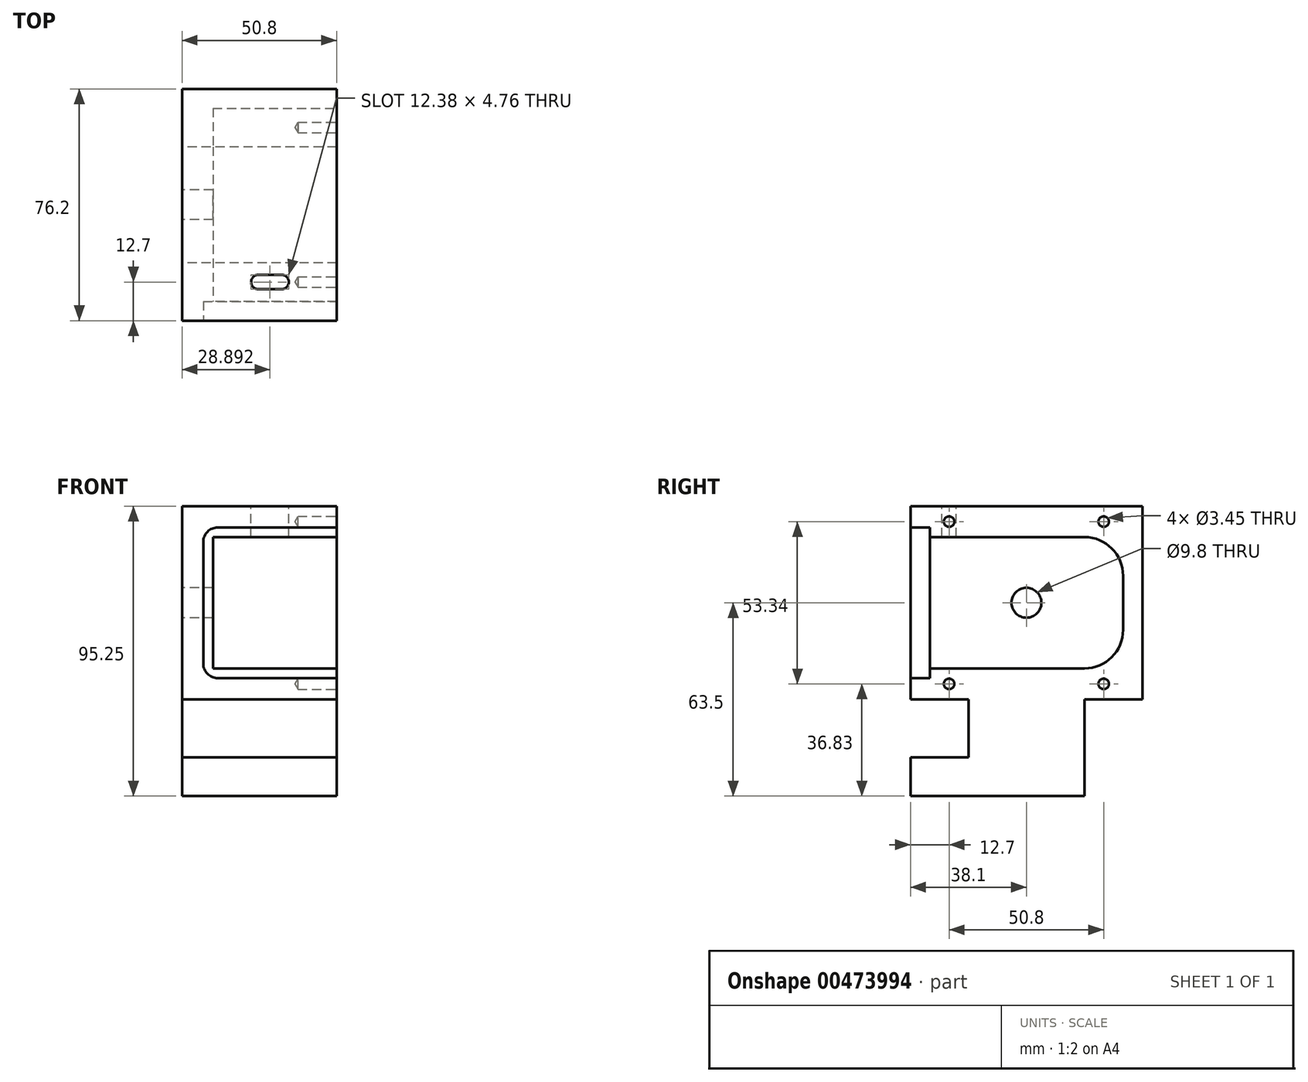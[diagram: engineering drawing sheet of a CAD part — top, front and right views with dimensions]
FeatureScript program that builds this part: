
annotation { "Feature Type Name" : "Feature", "Feature Type Description" : "" }
export const myFeature = defineFeature(function(context is Context, id is Id, definition is map)
    precondition{}
    {
        {
            var Q0;
            Q0=qCreatedBy(makeId("Right.planeOp"),FACE);
            var sketch = newSketch(context, id + "F0", { "sketchPlane" : qUnion([Q0])});
            skLineSegment(sketch, "E0.bottom", {"start": v(0, 0) * mm, "end": v(76.2, 0) * mm});
            skLineSegment(sketch, "E0.top", {"start": v(0, 63.5) * mm, "end": v(76.2, 63.5) * mm});
            skLineSegment(sketch, "E0.left", {"start": v(0, 0) * mm, "end": v(0, 63.5) * mm});
            skLineSegment(sketch, "E0.right", {"start": v(76.2, 0) * mm, "end": v(76.2, 63.5) * mm});
            skLineSegment(sketch, "E1.bottom", {"start": v(19.05, 0) * mm, "end": v(57.15, 0) * mm});
            skLineSegment(sketch, "E1.top", {"start": v(19.05, -19.05) * mm, "end": v(57.15, -19.05) * mm});
            skLineSegment(sketch, "E1.left", {"start": v(19.05, 0) * mm, "end": v(19.05, -19.05) * mm});
            skLineSegment(sketch, "E1.right", {"start": v(57.15, 0) * mm, "end": v(57.15, -19.05) * mm});
            skSolve(sketch);
        }
        {
            var Q0;
            Q0 = qSketchRegion(id + "F0", true);
            extrude(context, id + "F1", {"entities" : qUnion([Q0]), "depth" : 50.8 * mm});
        }
        {
            var Q0;
            Q0=makeQuery(id+"F1.opExtrude","CAP_FACE",FACE,{"disambiguationData":[OSD([sQuery(id+"F0.wireOp",EDGE,"E0.bottom"),sQuery(id+"F0.wireOp",EDGE,"E0.top"),sQuery(id+"F0.wireOp",EDGE,"E0.left"),sQuery(id+"F0.wireOp",EDGE,"E0.right"),sQuery(id+"F0.wireOp",EDGE,"E1.top"),sQuery(id+"F0.wireOp",EDGE,"E1.left"),sQuery(id+"F0.wireOp",EDGE,"E1.right")])],"isStart":true});
            var sketch = newSketch(context, id + "F2", { "sketchPlane" : qUnion([Q0])});
            skCircle(sketch, "E2", {"center": v(-38.1, 31.75) * mm, "radius": 11.22 * mm});
            skSolve(sketch);
        }
        {
            var Q0;
            Q0=sQuery(id+"F2.wireOp",VERTEX,"E2.center");
            var Q1;
            Q1=makeQuery(id+"F1.opExtrude","SWEPT_BODY",BODY,{"disambiguationData":[OSD([sQuery(id+"F0.wireOp",EDGE,"E0.bottom"),sQuery(id+"F0.wireOp",EDGE,"E0.top"),sQuery(id+"F0.wireOp",EDGE,"E0.left"),sQuery(id+"F0.wireOp",EDGE,"E0.right"),sQuery(id+"F0.wireOp",EDGE,"E1.top"),sQuery(id+"F0.wireOp",EDGE,"E1.left"),sQuery(id+"F0.wireOp",EDGE,"E1.right")])]});
            hole(context, id + "F3", {"style" : HoleStyle.SIMPLE, "endStyle" : HoleEndStyle.THROUGH, "standardTappedOrClearance" : lookupTablePath({ "standard" : "ANSI", "fit" : "Close", "size" : "3/8", "type" : "Clearance" }), "standardBlindInLast" : lookupTablePath({ "fit" : "Close", "standard" : "ANSI", "size" : "3/8", "type" : "Clearance" }), "holeDiameter" : 9.8 * mm, "isTappedThrough" : true, "tappedDepth" : 3.96 * mm, "tapClearance" : 3, "locations" : qUnion([Q0]), "scope" : qUnion([Q1])});
        }
        {
            var Q0;
            Q0=makeQuery(id+"F1.opExtrude","SWEPT_FACE",FACE,{"disambiguationData":[OSD([sQuery(id+"F0.wireOp",EDGE,"E1.top")])]});
            var sketch = newSketch(context, id + "F4", { "sketchPlane" : qUnion([Q0])});
            skLineSegment(sketch, "E3.0", {"start": v(50.8, -76.2) * mm, "end": v(0, -76.2) * mm});
            skLineSegment(sketch, "E4.0", {"start": v(50.8, -57.15) * mm, "end": v(50.8, -76.2) * mm});
            skLineSegment(sketch, "E5.0", {"start": v(50.8, -19.05) * mm, "end": v(50.8, -57.15) * mm});
            skLineSegment(sketch, "E6.0", {"start": v(50.8, 0) * mm, "end": v(50.8, -19.05) * mm});
            skLineSegment(sketch, "E7.bottom", {"start": v(0, 0) * mm, "end": v(50.8, 0) * mm});
            skLineSegment(sketch, "E7.top", {"start": v(0, -76.2) * mm, "end": v(50.8, -76.2) * mm});
            skLineSegment(sketch, "E7.left", {"start": v(0, 0) * mm, "end": v(0, -76.2) * mm});
            skLineSegment(sketch, "E7.right", {"start": v(50.8, 0) * mm, "end": v(50.8, -76.2) * mm});
            skSolve(sketch);
        }
        {
            var Q0;
            {var subQ0=sQuery(id+"F4.wireOp",EDGE,"E7.bottom");Q0=makeQuery(id+"F4.imprint","IMPRINT",FACE,{"disambiguationData":[TD([[makeQuery(id+"F4.imprint","IMPRINT",EDGE,{"derivedFrom":subQ0}),-1.0]])]});}
            var Q1;
            {var subQ0=sQuery(id+"F4.wireOp",EDGE,"E7.top");Q1=makeQuery(id+"F4.imprint","IMPRINT",FACE,{"disambiguationData":[TD([[makeQuery(id+"F4.imprint","IMPRINT",EDGE,{"derivedFrom":subQ0}),1.0]])]});}
            var Q2;
            {var subQ0=sQuery(id+"F0.wireOp",EDGE,"E1.top");var subQ3=makeQuery(id+"F1.opExtrude","SWEPT_EDGE",EDGE,{"disambiguationData":[OSD([subQ0,sQuery(id+"F0.wireOp",EDGE,"E1.left")])]});Q2=makeQuery(id+"F4.imprint","IMPRINT",FACE,{"disambiguationData":[TD([[makeQuery(id+"F4.imprint","IMPRINT",EDGE,{"derivedFrom":subQ3}),1.0]])]});}
            extrude(context, id + "F5", {"entities" : qUnion([Q0, Q1, Q2]), "operationType" : NewBodyOperationType.ADD, "depth" : 12.7 * mm});
        }
        {
            var Q0;
            Q0=makeQuery(id+"F1.opExtrude","SWEPT_FACE",FACE,{"disambiguationData":[OSD([sQuery(id+"F0.wireOp",EDGE,"E0.left")])]});
            var sketch = newSketch(context, id + "F6", { "sketchPlane" : qUnion([Q0])});
            skSolve(sketch);
        }
        {
            var Q0;
            {var subQ0=sQuery(id+"F0.wireOp",EDGE,"E0.left");Q0=makeQuery(id+"F6.imprint","IMPRINT",FACE,{"disambiguationData":[TD([[makeQuery(id+"F6.imprint","IMPRINT",EDGE,{"derivedFrom":makeQuery(id+"F1.opExtrude","CAP_EDGE",EDGE,{"disambiguationData":[OSD([subQ0])],"isStart":true})}),-1.0]])]});}
            var sketch = newSketch(context, id + "F7", { "sketchPlane" : qUnion([Q0])});
            skLineSegment(sketch, "E8.0.0", {"start": v(0, 63.5) * mm, "end": v(0, 0) * mm});
            skLineSegment(sketch, "E8.0.1", {"start": v(0, 0) * mm, "end": v(50.8, 0) * mm});
            skLineSegment(sketch, "E8.0.2", {"start": v(50.8, 0) * mm, "end": v(50.8, 63.5) * mm});
            skLineSegment(sketch, "E8.0.3", {"start": v(50.8, 63.5) * mm, "end": v(0, 63.5) * mm});
            skLineSegment(sketch, "E9.bottom", {"start": v(10.16, 53.34) * mm, "end": v(50.8, 53.34) * mm});
            skLineSegment(sketch, "E9.top", {"start": v(10.16, 10.16) * mm, "end": v(50.8, 10.16) * mm});
            skLineSegment(sketch, "E9.left", {"start": v(10.16, 53.34) * mm, "end": v(10.16, 10.16) * mm});
            skLineSegment(sketch, "E9.right", {"start": v(50.8, 53.34) * mm, "end": v(50.8, 10.16) * mm});
            skSolve(sketch);
        }
        {
            var Q0;
            Q0=makeQuery(id+"F7.imprint","IMPRINT",FACE,{"disambiguationData":[TD([[makeQuery(id+"F7.imprint","IMPRINT",EDGE,{"derivedFrom":sQuery(id+"F7.wireOp",EDGE,"E9.bottom")}),-1.0]])]});
            extrude(context, id + "F8", {"entities" : qUnion([Q0]), "operationType" : NewBodyOperationType.REMOVE, "oppositeDirection" : true, "depth" : 69.85 * mm});
        }
        {
            var Q0;
            {var subQ0=sQuery(id+"F0.wireOp",EDGE,"E0.left");Q0=makeQuery(id+"F6.imprint","IMPRINT",FACE,{"disambiguationData":[TD([[makeQuery(id+"F6.imprint","IMPRINT",EDGE,{"derivedFrom":makeQuery(id+"F1.opExtrude","CAP_EDGE",EDGE,{"disambiguationData":[OSD([subQ0])],"isStart":true})}),-1.0]])]});}
            var sketch = newSketch(context, id + "F9", { "sketchPlane" : qUnion([Q0])});
            skLineSegment(sketch, "E10.0.0", {"start": v(0, 63.5) * mm, "end": v(0, 0) * mm});
            skLineSegment(sketch, "E10.0.1", {"start": v(0, 0) * mm, "end": v(50.8, 0) * mm});
            skLineSegment(sketch, "E10.0.2", {"start": v(50.8, 0) * mm, "end": v(50.8, 63.5) * mm});
            skLineSegment(sketch, "E10.0.3", {"start": v(50.8, 63.5) * mm, "end": v(0, 63.5) * mm});
            skLineSegment(sketch, "E11.0", {"start": v(10.16, 53.34) * mm, "end": v(50.8, 53.34) * mm});
            skLineSegment(sketch, "E12.0", {"start": v(10.16, 53.34) * mm, "end": v(10.16, 10.16) * mm});
            skLineSegment(sketch, "E13.0", {"start": v(10.16, 10.16) * mm, "end": v(50.8, 10.16) * mm});
            skLineSegment(sketch, "E14.bottom", {"start": v(6.98, 56.51) * mm, "end": v(50.8, 56.51) * mm});
            skLineSegment(sketch, "E14.top", {"start": v(6.99, 6.99) * mm, "end": v(50.8, 6.99) * mm});
            skLineSegment(sketch, "E14.left", {"start": v(6.99, 56.51) * mm, "end": v(6.99, 6.99) * mm});
            skLineSegment(sketch, "E14.right", {"start": v(50.8, 56.51) * mm, "end": v(50.8, 6.99) * mm});
            skSolve(sketch);
        }
        {
            var Q0;
            {var subQ0=sQuery(id+"F9.wireOp",EDGE,"E11.0");Q0=makeQuery(id+"F9.imprint","IMPRINT",FACE,{"disambiguationData":[TD([[makeQuery(id+"F9.imprint","IMPRINT",EDGE,{"derivedFrom":subQ0}),-1.0]])]});}
            var Q1;
            {var subQ2=sQuery(id+"F9.wireOp",EDGE,"E11.0");Q1=makeQuery(id+"F9.imprint","IMPRINT",FACE,{"disambiguationData":[TD([[makeQuery(id+"F9.imprint","IMPRINT",EDGE,{"derivedFrom":subQ2}),1.0]])]});}
            extrude(context, id + "F10", {"entities" : qUnion([Q0, Q1]), "operationType" : NewBodyOperationType.REMOVE, "oppositeDirection" : true, "depth" : 6.35 * mm});
        }
        {
            var Q0;
            Q0=makeQuery(id+"F5.boolean.opBoolean","MERGE",FACE,{"derivedFrom":[makeQuery(id+"F1.opExtrude","CAP_FACE",FACE,{"disambiguationData":[OSD([sQuery(id+"F0.wireOp",EDGE,"E0.bottom"),sQuery(id+"F0.wireOp",EDGE,"E0.top"),sQuery(id+"F0.wireOp",EDGE,"E0.left"),sQuery(id+"F0.wireOp",EDGE,"E0.right"),sQuery(id+"F0.wireOp",EDGE,"E1.top"),sQuery(id+"F0.wireOp",EDGE,"E1.left"),sQuery(id+"F0.wireOp",EDGE,"E1.right")])],"isStart":false}),makeQuery(id+"F5.opExtrude","SWEPT_FACE",FACE,{"disambiguationData":[OSD([sQuery(id+"F4.wireOp",EDGE,"E7.right")])]})]});
            var sketch = newSketch(context, id + "F11", { "sketchPlane" : qUnion([Q0])});
            skLineSegment(sketch, "E15.bottom", {"start": v(0, -19.05) * mm, "end": v(76.2, -19.05) * mm});
            skLineSegment(sketch, "E15.top", {"start": v(0, -31.75) * mm, "end": v(76.2, -31.75) * mm});
            skLineSegment(sketch, "E15.left", {"start": v(0, -19.05) * mm, "end": v(0, -31.75) * mm});
            skLineSegment(sketch, "E15.right", {"start": v(76.2, -19.05) * mm, "end": v(76.2, -31.75) * mm});
            skSolve(sketch);
        }
        {
            var Q0;
            Q0=makeQuery(id+"F11.imprint","IMPRINT",FACE,{"disambiguationData":[TD([[makeQuery(id+"F11.imprint","IMPRINT",EDGE,{"derivedFrom":sQuery(id+"F11.wireOp",EDGE,"E15.top")}),1.0]])]});
            extrude(context, id + "F12", {"entities" : qUnion([Q0]), "operationType" : NewBodyOperationType.REMOVE, "oppositeDirection" : true, "depth" : 9.52 * mm});
        }
        {
            var Q0;
            Q0=makeQuery(id+"F5.boolean.opBoolean","MERGE",FACE,{"derivedFrom":[makeQuery(id+"F1.opExtrude","CAP_FACE",FACE,{"disambiguationData":[OSD([sQuery(id+"F0.wireOp",EDGE,"E0.bottom"),sQuery(id+"F0.wireOp",EDGE,"E0.top"),sQuery(id+"F0.wireOp",EDGE,"E0.left"),sQuery(id+"F0.wireOp",EDGE,"E0.right"),sQuery(id+"F0.wireOp",EDGE,"E1.top"),sQuery(id+"F0.wireOp",EDGE,"E1.left"),sQuery(id+"F0.wireOp",EDGE,"E1.right")])],"isStart":false}),makeQuery(id+"F5.opExtrude","SWEPT_FACE",FACE,{"disambiguationData":[OSD([sQuery(id+"F4.wireOp",EDGE,"E7.right")])]})]});
            var sketch = newSketch(context, id + "F13", { "sketchPlane" : qUnion([Q0])});
            skPoint(sketch, "E16", {"position": v(12.7, 58.42) * mm});
            skPoint(sketch, "E17", {"position": v(63.5, 58.42) * mm});
            skPoint(sketch, "E18", {"position": v(12.7, 5.08) * mm});
            skPoint(sketch, "E19", {"position": v(63.5, 5.08) * mm});
            skSolve(sketch);
        }
        {
            var Q0;
            Q0=sQuery(id+"F13.wireOp",VERTEX,"E16");
            var Q1;
            Q1=sQuery(id+"F13.wireOp",VERTEX,"E17");
            var Q2;
            Q2=sQuery(id+"F13.wireOp",VERTEX,"E18");
            var Q3;
            Q3=sQuery(id+"F13.wireOp",VERTEX,"E19");
            var Q4;
            Q4=makeQuery(id+"F1.opExtrude","SWEPT_BODY",BODY,{"disambiguationData":[OSD([sQuery(id+"F0.wireOp",EDGE,"E0.bottom"),sQuery(id+"F0.wireOp",EDGE,"E0.top"),sQuery(id+"F0.wireOp",EDGE,"E0.left"),sQuery(id+"F0.wireOp",EDGE,"E0.right"),sQuery(id+"F0.wireOp",EDGE,"E1.top"),sQuery(id+"F0.wireOp",EDGE,"E1.left"),sQuery(id+"F0.wireOp",EDGE,"E1.right")])]});
            hole(context, id + "F14", {"style" : HoleStyle.SIMPLE, "endStyle" : HoleEndStyle.BLIND, "standardTappedOrClearance" : lookupTablePath({ "standard" : "ANSI", "engagement" : "75%", "pitch" : "32 tpi", "size" : "#8", "type" : "Tapped" }), "standardBlindInLast" : lookupTablePath({ "standard" : "ANSI", "engagement" : "75%", "pitch" : "32 tpi", "size" : "#8", "type" : "Tapped" }), "holeDiameter" : 3.45 * mm, "showTappedDepth" : true, "holeDepth" : 12.7 * mm, "isTappedThrough" : true, "tappedDepth" : 10.32 * mm, "tapClearance" : 3, "locations" : qUnion([Q0, Q1, Q2, Q3]), "scope" : qUnion([Q4]), "majorDiameter" : 4.17 * mm});
        }
        {
            var Q0;
            Q0=makeQuery(id+"F8.boolean.opBoolean","COPY",EDGE,{"derivedFrom":makeQuery(id+"F8.opExtrude","CAP_EDGE",EDGE,{"disambiguationData":[OSD([sQuery(id+"F7.wireOp",EDGE,"E9.bottom")])],"isStart":false})});
            fillet(context, id + "F15", {"entities" : qUnion([Q0]), "radius" : 12.7 * mm, "tangentPropagation" : true, "allowEdgeOverflow" : false});
        }
        {
            var Q0;
            Q0=makeQuery(id+"F8.boolean.opBoolean","COPY",EDGE,{"derivedFrom":makeQuery(id+"F8.opExtrude","CAP_EDGE",EDGE,{"disambiguationData":[OSD([sQuery(id+"F7.wireOp",EDGE,"E9.top")])],"isStart":false})});
            fillet(context, id + "F16", {"entities" : qUnion([Q0]), "radius" : 12.7 * mm, "tangentPropagation" : true, "allowEdgeOverflow" : false});
        }
        {
            var Q0;
            Q0=makeQuery(id+"F10.boolean.opBoolean","COPY",EDGE,{"derivedFrom":makeQuery(id+"F10.opExtrude","SWEPT_EDGE",EDGE,{"disambiguationData":[OSD([sQuery(id+"F9.wireOp",EDGE,"E14.bottom"),sQuery(id+"F9.wireOp",EDGE,"E14.left")])]})});
            var Q1;
            Q1=makeQuery(id+"F10.boolean.opBoolean","COPY",EDGE,{"derivedFrom":makeQuery(id+"F10.opExtrude","SWEPT_EDGE",EDGE,{"disambiguationData":[OSD([sQuery(id+"F9.wireOp",EDGE,"E14.top"),sQuery(id+"F9.wireOp",EDGE,"E14.left")])]})});
            fillet(context, id + "F17", {"entities" : qUnion([Q0, Q1]), "radius" : 4.76 * mm, "tangentPropagation" : true, "allowEdgeOverflow" : false});
        }
        {
            var Q0;
            Q0=makeQuery(id+"F1.opExtrude","SWEPT_FACE",FACE,{"disambiguationData":[OSD([sQuery(id+"F0.wireOp",EDGE,"E0.top")])]});
            var sketch = newSketch(context, id + "F18", { "sketchPlane" : qUnion([Q0])});
            skCircle(sketch, "E20", {"center": v(25.08, 12.7) * mm, "radius": 2.38 * mm});
            skCircle(sketch, "E21", {"center": v(32.7, 12.7) * mm, "radius": 2.38 * mm});
            skLineSegment(sketch, "E22", {"start": v(25.08, 15.08) * mm, "end": v(32.7, 15.08) * mm});
            skLineSegment(sketch, "E23", {"start": v(25.08, 10.32) * mm, "end": v(32.7, 10.32) * mm});
            skPoint(sketch, "E24", {"position": v(28.9, 12.7) * mm});
            skSolve(sketch);
        }
        {
            var Q0;
            {var subQ0=sQuery(id+"F18.wireOp",EDGE,"E22");Q0=makeQuery(id+"F18.imprint","IMPRINT",FACE,{"disambiguationData":[TD([[makeQuery(id+"F18.imprint","IMPRINT",EDGE,{"derivedFrom":subQ0}),-1.0]])]});}
            var Q1;
            {var subQ0=sQuery(id+"F18.wireOp",EDGE,"E21");var subQ1=makeQuery(id+"F18.imprint","INTERSECT",VERTEX,{"derivedFrom":[subQ0,sQuery(id+"F18.wireOp",EDGE,"E22")]});Q1=makeQuery(id+"F18.imprint","IMPRINT",FACE,{"disambiguationData":[TD([[makeQuery(id+"F18.imprint","IMPRINT",EDGE,{"disambiguationData":[TD([[subQ1,-1.0]])],"derivedFrom":subQ0}),1.0]])]});}
            var Q2;
            {var subQ0=sQuery(id+"F18.wireOp",EDGE,"E20");var subQ1=makeQuery(id+"F18.imprint","INTERSECT",VERTEX,{"derivedFrom":[subQ0,sQuery(id+"F18.wireOp",EDGE,"E22")]});Q2=makeQuery(id+"F18.imprint","IMPRINT",FACE,{"disambiguationData":[TD([[makeQuery(id+"F18.imprint","IMPRINT",EDGE,{"disambiguationData":[TD([[subQ1,-1.0]])],"derivedFrom":subQ0}),1.0]])]});}
            extrude(context, id + "F19", {"entities" : qUnion([Q0, Q1, Q2]), "operationType" : NewBodyOperationType.REMOVE, "oppositeDirection" : true, "depth" : 25.4 * mm});
        }
    });
